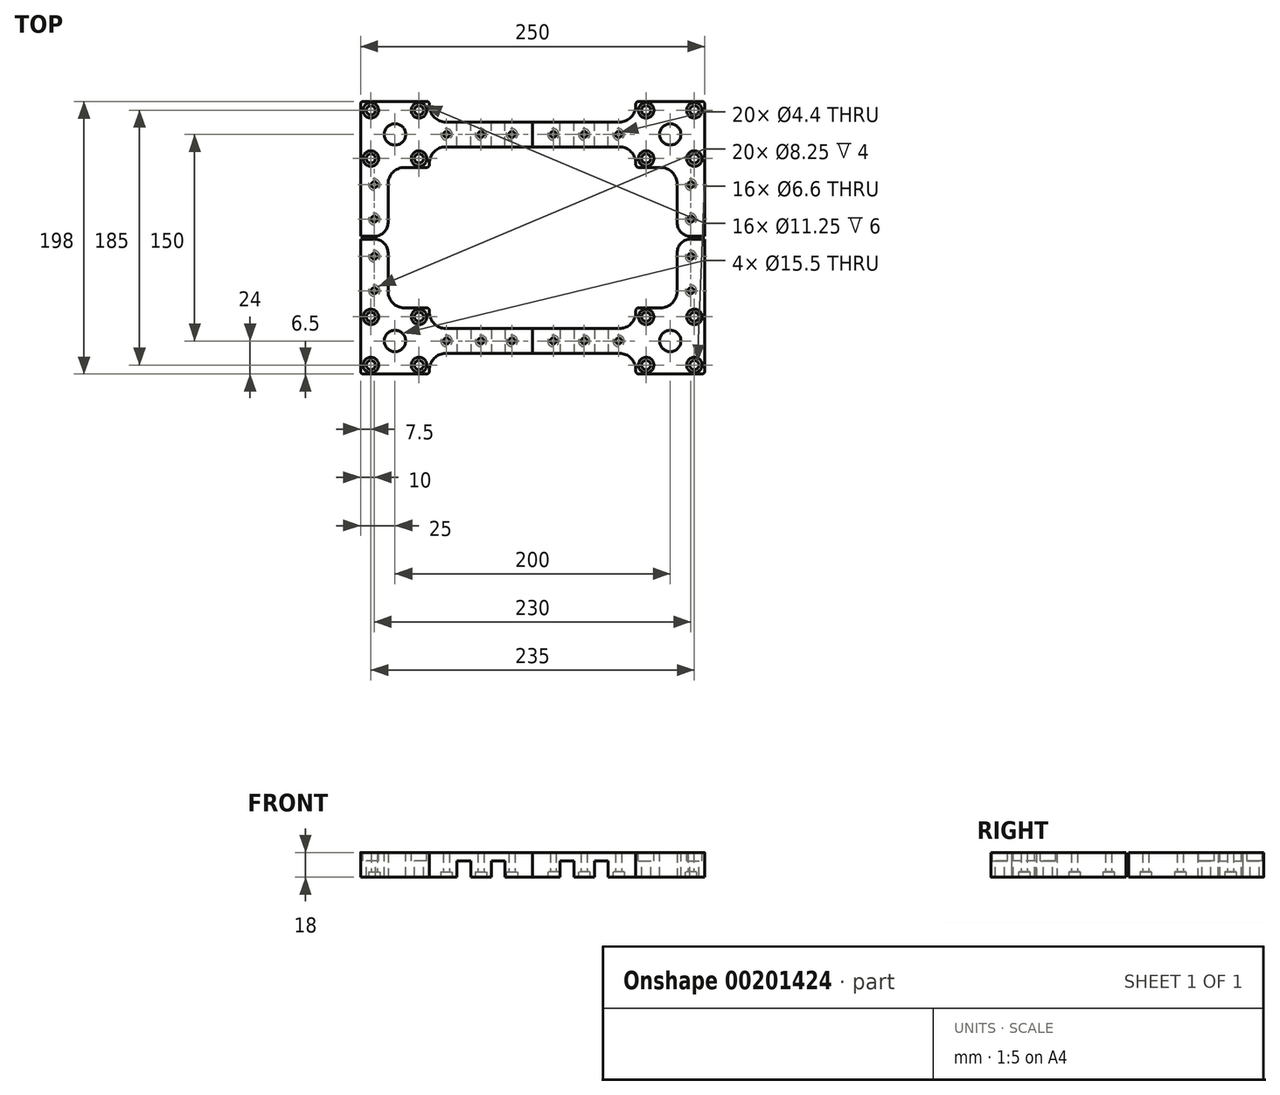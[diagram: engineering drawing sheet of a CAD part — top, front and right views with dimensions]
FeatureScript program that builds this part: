
annotation { "Feature Type Name" : "Feature", "Feature Type Description" : "" }
export const myFeature = defineFeature(function(context is Context, id is Id, definition is map)
    precondition{}
    {
        {
            var Q0;
            Q0=qCreatedBy(makeId("Top.planeOp"),FACE);
            var sketch = newSketch(context, id + "F0", { "sketchPlane" : qUnion([Q0])});
            skLineSegment(sketch, "E0", {"start": v(-125, 0) * mm, "end": v(-125, 24) * mm});
            skLineSegment(sketch, "E1", {"start": v(-105, 24) * mm, "end": v(-75, 24) * mm});
            skLineSegment(sketch, "E2", {"start": v(-75, 24) * mm, "end": v(-75, 9) * mm});
            skLineSegment(sketch, "E3", {"start": v(-75, 9) * mm, "end": v(0, 9) * mm});
            skLineSegment(sketch, "E4", {"start": v(0, 9) * mm, "end": v(0, 0) * mm});
            skLineSegment(sketch, "E5", {"start": v(-125, 24) * mm, "end": v(-125, 74) * mm});
            skLineSegment(sketch, "E6", {"start": v(-105, 74) * mm, "end": v(-125, 74) * mm});
            skLineSegment(sketch, "E7", {"start": v(-105, 74) * mm, "end": v(-105, 24) * mm});
            skLineSegment(sketch, "E8.MirrorCS", {"start": v(-75, -24) * mm, "end": v(-75, -9) * mm});
            skLineSegment(sketch, "E9.MirrorCS", {"start": v(-75, -9) * mm, "end": v(0, -9) * mm});
            skLineSegment(sketch, "E10.MirrorCS", {"start": v(-125, -24) * mm, "end": v(-75, -24) * mm});
            skLineSegment(sketch, "E11.MirrorCS", {"start": v(0, -9) * mm, "end": v(0, 0) * mm});
            skLineSegment(sketch, "E12.MirrorCS", {"start": v(-125, 0) * mm, "end": v(-125, -24) * mm});
            skSolve(sketch);
        }
        {
            var Q0;
            Q0=makeQuery(id+"F0.imprint","IMPRINT",FACE,{"disambiguationData":[TD([[makeQuery(id+"F0.imprint","IMPRINT",EDGE,{"derivedFrom":sQuery(id+"F0.wireOp",EDGE,"E0")}),-1.0]])]});
            extrude(context, id + "F1", {"entities" : qUnion([Q0]), "depth" : 18 * mm});
        }
        {
            var Q0;
            Q0=makeQuery(id+"F1.opExtrude","CAP_FACE",FACE,{"disambiguationData":[OSD([sQuery(id+"F0.wireOp",EDGE,"E0"),sQuery(id+"F0.wireOp",EDGE,"E1"),sQuery(id+"F0.wireOp",EDGE,"E2"),sQuery(id+"F0.wireOp",EDGE,"E3"),sQuery(id+"F0.wireOp",EDGE,"E4"),sQuery(id+"F0.wireOp",EDGE,"E5"),sQuery(id+"F0.wireOp",EDGE,"E6"),sQuery(id+"F0.wireOp",EDGE,"E7"),sQuery(id+"F0.wireOp",EDGE,"E8.MirrorCS"),sQuery(id+"F0.wireOp",EDGE,"E9.MirrorCS"),sQuery(id+"F0.wireOp",EDGE,"E10.MirrorCS"),sQuery(id+"F0.wireOp",EDGE,"E11.MirrorCS"),sQuery(id+"F0.wireOp",EDGE,"E12.MirrorCS")])],"isStart":false});
            var sketch = newSketch(context, id + "F2", { "sketchPlane" : qUnion([Q0])});
            skPoint(sketch, "E13", {"position": v(-117.5, 17.5) * mm});
            skPoint(sketch, "E14", {"position": v(-82.5, 17.5) * mm});
            skPoint(sketch, "E15", {"position": v(-82.5, -17.5) * mm});
            skPoint(sketch, "E16", {"position": v(-117.5, -17.5) * mm});
            skPoint(sketch, "E17", {"position": v(-100, 0) * mm});
            skPoint(sketch, "E18", {"position": v(-15, 0) * mm});
            skPoint(sketch, "E19", {"position": v(-37.5, 0) * mm});
            skPoint(sketch, "E20", {"position": v(-62.5, 0) * mm});
            skPoint(sketch, "E21", {"position": v(-115, 61.5) * mm});
            skPoint(sketch, "E22", {"position": v(-115, 36.5) * mm});
            skSolve(sketch);
        }
        {
            var Q0;
            Q0=sQuery(id+"F2.wireOp",VERTEX,"E13");
            var Q1;
            Q1=sQuery(id+"F2.wireOp",VERTEX,"E14");
            var Q2;
            Q2=sQuery(id+"F2.wireOp",VERTEX,"E15");
            var Q3;
            Q3=sQuery(id+"F2.wireOp",VERTEX,"E16");
            var Q4;
            Q4=makeQuery(id+"F1.opExtrude","SWEPT_BODY",BODY,{"disambiguationData":[OSD([sQuery(id+"F0.wireOp",EDGE,"E0"),sQuery(id+"F0.wireOp",EDGE,"E1"),sQuery(id+"F0.wireOp",EDGE,"E2"),sQuery(id+"F0.wireOp",EDGE,"E3"),sQuery(id+"F0.wireOp",EDGE,"E4"),sQuery(id+"F0.wireOp",EDGE,"E5"),sQuery(id+"F0.wireOp",EDGE,"E6"),sQuery(id+"F0.wireOp",EDGE,"E7"),sQuery(id+"F0.wireOp",EDGE,"E8.MirrorCS"),sQuery(id+"F0.wireOp",EDGE,"E9.MirrorCS"),sQuery(id+"F0.wireOp",EDGE,"E10.MirrorCS"),sQuery(id+"F0.wireOp",EDGE,"E11.MirrorCS"),sQuery(id+"F0.wireOp",EDGE,"E12.MirrorCS")])]});
            hole(context, id + "F3", {"style" : HoleStyle.C_BORE, "endStyle" : HoleEndStyle.THROUGH, "standardTappedOrClearance" : lookupTablePath({ "standard" : "ISO", "fit" : "Normal", "size" : "M6", "type" : "Clearance" }), "standardBlindInLast" : lookupTablePath({ "fit" : "Standard", "standard" : "ISO", "size" : "M6", "type" : "Clearance" }), "holeDiameter" : 6.6 * mm, "cBoreDiameter" : 11.25 * mm, "cBoreDepth" : 6 * mm, "startFromSketch" : true, "locations" : qUnion([Q0, Q1, Q2, Q3]), "scope" : qUnion([Q4]), "isTappedThrough" : true});
        }
        {
            var Q0;
            Q0=makeQuery(id+"F1.opExtrude","CAP_FACE",FACE,{"disambiguationData":[OSD([sQuery(id+"F0.wireOp",EDGE,"E0"),sQuery(id+"F0.wireOp",EDGE,"E1"),sQuery(id+"F0.wireOp",EDGE,"E2"),sQuery(id+"F0.wireOp",EDGE,"E3"),sQuery(id+"F0.wireOp",EDGE,"E4"),sQuery(id+"F0.wireOp",EDGE,"E5"),sQuery(id+"F0.wireOp",EDGE,"E6"),sQuery(id+"F0.wireOp",EDGE,"E7"),sQuery(id+"F0.wireOp",EDGE,"E8.MirrorCS"),sQuery(id+"F0.wireOp",EDGE,"E9.MirrorCS"),sQuery(id+"F0.wireOp",EDGE,"E10.MirrorCS"),sQuery(id+"F0.wireOp",EDGE,"E11.MirrorCS"),sQuery(id+"F0.wireOp",EDGE,"E12.MirrorCS")])],"isStart":true});
            var sketch = newSketch(context, id + "F4", { "sketchPlane" : qUnion([Q0])});
            skPoint(sketch, "E23", {"position": v(-62.5, 0) * mm});
            skPoint(sketch, "E24", {"position": v(-37.5, 0) * mm});
            skPoint(sketch, "E25", {"position": v(-15, 0) * mm});
            skPoint(sketch, "E26", {"position": v(-115, -36.5) * mm});
            skPoint(sketch, "E27", {"position": v(-115, -61.5) * mm});
            skSolve(sketch);
        }
        {
            var Q0;
            Q0=sQuery(id+"F4.wireOp",VERTEX,"E23");
            var Q1;
            Q1=sQuery(id+"F4.wireOp",VERTEX,"E24");
            var Q2;
            Q2=sQuery(id+"F4.wireOp",VERTEX,"E25");
            var Q3;
            Q3=sQuery(id+"F4.wireOp",VERTEX,"E26");
            var Q4;
            Q4=sQuery(id+"F4.wireOp",VERTEX,"E27");
            var Q5;
            Q5=makeQuery(id+"F1.opExtrude","SWEPT_BODY",BODY,{"disambiguationData":[OSD([sQuery(id+"F0.wireOp",EDGE,"E0"),sQuery(id+"F0.wireOp",EDGE,"E1"),sQuery(id+"F0.wireOp",EDGE,"E2"),sQuery(id+"F0.wireOp",EDGE,"E3"),sQuery(id+"F0.wireOp",EDGE,"E4"),sQuery(id+"F0.wireOp",EDGE,"E5"),sQuery(id+"F0.wireOp",EDGE,"E6"),sQuery(id+"F0.wireOp",EDGE,"E7"),sQuery(id+"F0.wireOp",EDGE,"E8.MirrorCS"),sQuery(id+"F0.wireOp",EDGE,"E9.MirrorCS"),sQuery(id+"F0.wireOp",EDGE,"E10.MirrorCS"),sQuery(id+"F0.wireOp",EDGE,"E11.MirrorCS"),sQuery(id+"F0.wireOp",EDGE,"E12.MirrorCS")])]});
            hole(context, id + "F5", {"style" : HoleStyle.C_BORE, "endStyle" : HoleEndStyle.THROUGH, "standardTappedOrClearance" : lookupTablePath({ "standard" : "ISO", "fit" : "Normal", "size" : "M4", "type" : "Clearance" }), "standardBlindInLast" : lookupTablePath({ "fit" : "Standard", "standard" : "ISO", "size" : "M4", "type" : "Clearance" }), "holeDiameter" : 4.4 * mm, "cBoreDiameter" : 8.25 * mm, "cBoreDepth" : 4 * mm, "startFromSketch" : true, "locations" : qUnion([Q0, Q1, Q2, Q3, Q4]), "scope" : qUnion([Q5]), "isTappedThrough" : true});
        }
        {
            var Q0;
            Q0=sQuery(id+"F2.wireOp",VERTEX,"E17");
            var Q1;
            Q1=makeQuery(id+"F1.opExtrude","SWEPT_BODY",BODY,{"disambiguationData":[OSD([sQuery(id+"F0.wireOp",EDGE,"E0"),sQuery(id+"F0.wireOp",EDGE,"E1"),sQuery(id+"F0.wireOp",EDGE,"E2"),sQuery(id+"F0.wireOp",EDGE,"E3"),sQuery(id+"F0.wireOp",EDGE,"E4"),sQuery(id+"F0.wireOp",EDGE,"E5"),sQuery(id+"F0.wireOp",EDGE,"E6"),sQuery(id+"F0.wireOp",EDGE,"E7"),sQuery(id+"F0.wireOp",EDGE,"E8.MirrorCS"),sQuery(id+"F0.wireOp",EDGE,"E9.MirrorCS"),sQuery(id+"F0.wireOp",EDGE,"E10.MirrorCS"),sQuery(id+"F0.wireOp",EDGE,"E11.MirrorCS"),sQuery(id+"F0.wireOp",EDGE,"E12.MirrorCS")])]});
            hole(context, id + "F6", {"style" : HoleStyle.SIMPLE, "endStyle" : HoleEndStyle.THROUGH, "standardTappedOrClearance" : lookupTablePath({ "standard" : "ISO", "fit" : "Normal", "size" : "M14", "type" : "Clearance" }), "standardBlindInLast" : lookupTablePath({ "fit" : "Standard", "standard" : "ISO", "size" : "M14", "type" : "Clearance" }), "holeDiameter" : 15.5 * mm, "startFromSketch" : true, "locations" : qUnion([Q0]), "scope" : qUnion([Q1]), "isTappedThrough" : true});
        }
        {
            var Q0;
            Q0=makeQuery(id+"F1.opExtrude","SWEPT_EDGE",EDGE,{"disambiguationData":[OSD([sQuery(id+"F0.wireOp",EDGE,"E1"),sQuery(id+"F0.wireOp",EDGE,"E7")])]});
            var Q1;
            Q1=makeQuery(id+"F1.opExtrude","SWEPT_EDGE",EDGE,{"disambiguationData":[OSD([sQuery(id+"F0.wireOp",EDGE,"E8.MirrorCS"),sQuery(id+"F0.wireOp",EDGE,"E9.MirrorCS")])]});
            var Q2;
            Q2=makeQuery(id+"F1.opExtrude","SWEPT_EDGE",EDGE,{"disambiguationData":[OSD([sQuery(id+"F0.wireOp",EDGE,"E2"),sQuery(id+"F0.wireOp",EDGE,"E3")])]});
            fillet(context, id + "F7", {"entities" : qUnion([Q0, Q1, Q2]), "radius" : 12 * mm, "tangentPropagation" : true, "allowEdgeOverflow" : false});
        }
        {
            var Q0;
            Q0=makeQuery(id+"F1.opExtrude","SWEPT_EDGE",EDGE,{"disambiguationData":[OSD([sQuery(id+"F0.wireOp",EDGE,"E6"),sQuery(id+"F0.wireOp",EDGE,"E7")])]});
            fillet(context, id + "F8", {"entities" : qUnion([Q0]), "radius" : 10 * mm, "tangentPropagation" : true, "allowEdgeOverflow" : false});
        }
        {
            var Q0;
            Q0=makeQuery(id+"F1.opExtrude","SWEPT_EDGE",EDGE,{"disambiguationData":[OSD([sQuery(id+"F0.wireOp",EDGE,"E1"),sQuery(id+"F0.wireOp",EDGE,"E2")])]});
            fillet(context, id + "F9", {"entities" : qUnion([Q0]), "radius" : 2 * mm, "tangentPropagation" : true, "allowEdgeOverflow" : false});
        }
        {
            var Q0;
            Q0=makeQuery(id+"F1.opExtrude","SWEPT_EDGE",EDGE,{"disambiguationData":[OSD([sQuery(id+"F0.wireOp",EDGE,"E8.MirrorCS"),sQuery(id+"F0.wireOp",EDGE,"E10.MirrorCS")])]});
            var Q1;
            Q1=makeQuery(id+"F1.opExtrude","SWEPT_EDGE",EDGE,{"disambiguationData":[OSD([sQuery(id+"F0.wireOp",EDGE,"E10.MirrorCS"),sQuery(id+"F0.wireOp",EDGE,"E12.MirrorCS")])]});
            fillet(context, id + "F10", {"entities" : qUnion([Q0, Q1]), "radius" : 2 * mm, "tangentPropagation" : true, "allowEdgeOverflow" : false});
        }
        {
            var Q0;
            Q0=makeQuery(id+"F1.opExtrude","SWEPT_FACE",FACE,{"disambiguationData":[OSD([sQuery(id+"F0.wireOp",EDGE,"E9.MirrorCS")])]});
            var sketch = newSketch(context, id + "F11", { "sketchPlane" : qUnion([Q0])});
            skLineSegment(sketch, "E28.bottom", {"start": v(-55, 12) * mm, "end": v(-45, 12) * mm});
            skLineSegment(sketch, "E28.top", {"start": v(-55, 0) * mm, "end": v(-45, 0) * mm});
            skLineSegment(sketch, "E28.left", {"start": v(-55, 12) * mm, "end": v(-55, 0) * mm});
            skLineSegment(sketch, "E28.right", {"start": v(-45, 12) * mm, "end": v(-45, 0) * mm});
            skLineSegment(sketch, "E29.1.0.0", {"start": v(-20, 12) * mm, "end": v(-20, 0) * mm});
            skLineSegment(sketch, "E29.1.0.1", {"start": v(-30, 0) * mm, "end": v(-20, 0) * mm});
            skLineSegment(sketch, "E29.1.0.2", {"start": v(-30, 12) * mm, "end": v(-30, 0) * mm});
            skLineSegment(sketch, "E29.1.0.3", {"start": v(-30, 12) * mm, "end": v(-20, 12) * mm});
            skLineSegment(sketch, "E29.direction1", {"start": v(-55, 0) * mm, "end": v(-30, 0) * mm, "construction": true});
            skSolve(sketch);
        }
        {
            var Q0;
            Q0=makeQuery(id+"F11.imprint","IMPRINT",FACE,{"disambiguationData":[TD([[makeQuery(id+"F11.imprint","IMPRINT",EDGE,{"derivedFrom":sQuery(id+"F11.wireOp",EDGE,"E28.bottom")}),-1.0]])]});
            var Q1;
            Q1=makeQuery(id+"F11.imprint","IMPRINT",FACE,{"disambiguationData":[TD([[makeQuery(id+"F11.imprint","IMPRINT",EDGE,{"derivedFrom":sQuery(id+"F11.wireOp",EDGE,"E29.1.0.0")}),-1.0]])]});
            extrude(context, id + "F12", {"entities" : qUnion([Q0, Q1]), "operationType" : NewBodyOperationType.REMOVE, "endBound" : BoundingType.THROUGH_ALL, "oppositeDirection" : true, "depth" : 25 * mm});
        }
        {
            var Q0;
            Q0=makeQuery(id+"F1.opExtrude","SWEPT_BODY",BODY,{"disambiguationData":[OSD([sQuery(id+"F0.wireOp",EDGE,"E0"),sQuery(id+"F0.wireOp",EDGE,"E1"),sQuery(id+"F0.wireOp",EDGE,"E2"),sQuery(id+"F0.wireOp",EDGE,"E3"),sQuery(id+"F0.wireOp",EDGE,"E4"),sQuery(id+"F0.wireOp",EDGE,"E5"),sQuery(id+"F0.wireOp",EDGE,"E6"),sQuery(id+"F0.wireOp",EDGE,"E7"),sQuery(id+"F0.wireOp",EDGE,"E8.MirrorCS"),sQuery(id+"F0.wireOp",EDGE,"E9.MirrorCS"),sQuery(id+"F0.wireOp",EDGE,"E10.MirrorCS"),sQuery(id+"F0.wireOp",EDGE,"E11.MirrorCS"),sQuery(id+"F0.wireOp",EDGE,"E12.MirrorCS")])]});
            var Q1;
            Q1=qCreatedBy(makeId("Right.planeOp"),FACE);
            mirror(context, id + "F13", {"entities" : qUnion([Q0]), "mirrorPlane" : qUnion([Q1])});
        }
        {
            var Q0;
            Q0=makeQuery(id+"F1.opExtrude","SWEPT_BODY",BODY,{"disambiguationData":[OSD([sQuery(id+"F0.wireOp",EDGE,"E0"),sQuery(id+"F0.wireOp",EDGE,"E1"),sQuery(id+"F0.wireOp",EDGE,"E2"),sQuery(id+"F0.wireOp",EDGE,"E3"),sQuery(id+"F0.wireOp",EDGE,"E4"),sQuery(id+"F0.wireOp",EDGE,"E5"),sQuery(id+"F0.wireOp",EDGE,"E6"),sQuery(id+"F0.wireOp",EDGE,"E7"),sQuery(id+"F0.wireOp",EDGE,"E8.MirrorCS"),sQuery(id+"F0.wireOp",EDGE,"E9.MirrorCS"),sQuery(id+"F0.wireOp",EDGE,"E10.MirrorCS"),sQuery(id+"F0.wireOp",EDGE,"E11.MirrorCS"),sQuery(id+"F0.wireOp",EDGE,"E12.MirrorCS")])]});
            var Q1;
            Q1=qCreatedBy(makeId("Front.planeOp"),FACE);
            mirror(context, id + "F14", {"entities" : qUnion([Q0]), "mirrorPlane" : qUnion([Q1])});
        }
        {
            var Q0;
            Q0=makeQuery(id+"F13.opPattern","COPY",BODY,{"derivedFrom":makeQuery(id+"F1.opExtrude","SWEPT_BODY",BODY,{"disambiguationData":[OSD([sQuery(id+"F0.wireOp",EDGE,"E0"),sQuery(id+"F0.wireOp",EDGE,"E1"),sQuery(id+"F0.wireOp",EDGE,"E2"),sQuery(id+"F0.wireOp",EDGE,"E3"),sQuery(id+"F0.wireOp",EDGE,"E4"),sQuery(id+"F0.wireOp",EDGE,"E5"),sQuery(id+"F0.wireOp",EDGE,"E6"),sQuery(id+"F0.wireOp",EDGE,"E7"),sQuery(id+"F0.wireOp",EDGE,"E8.MirrorCS"),sQuery(id+"F0.wireOp",EDGE,"E9.MirrorCS"),sQuery(id+"F0.wireOp",EDGE,"E10.MirrorCS"),sQuery(id+"F0.wireOp",EDGE,"E11.MirrorCS"),sQuery(id+"F0.wireOp",EDGE,"E12.MirrorCS")])]}),"instanceName":"1"});
            var Q1;
            Q1=qCreatedBy(makeId("Front.planeOp"),FACE);
            mirror(context, id + "F15", {"entities" : qUnion([Q0]), "mirrorPlane" : qUnion([Q1])});
        }
        {
            var Q0;
            Q0=makeQuery(id+"F13.opPattern","COPY",BODY,{"derivedFrom":makeQuery(id+"F1.opExtrude","SWEPT_BODY",BODY,{"disambiguationData":[OSD([sQuery(id+"F0.wireOp",EDGE,"E0"),sQuery(id+"F0.wireOp",EDGE,"E1"),sQuery(id+"F0.wireOp",EDGE,"E2"),sQuery(id+"F0.wireOp",EDGE,"E3"),sQuery(id+"F0.wireOp",EDGE,"E4"),sQuery(id+"F0.wireOp",EDGE,"E5"),sQuery(id+"F0.wireOp",EDGE,"E6"),sQuery(id+"F0.wireOp",EDGE,"E7"),sQuery(id+"F0.wireOp",EDGE,"E8.MirrorCS"),sQuery(id+"F0.wireOp",EDGE,"E9.MirrorCS"),sQuery(id+"F0.wireOp",EDGE,"E10.MirrorCS"),sQuery(id+"F0.wireOp",EDGE,"E11.MirrorCS"),sQuery(id+"F0.wireOp",EDGE,"E12.MirrorCS")])]}),"instanceName":"1"});
            transform(context, id + "F16", {"entities" : qUnion([Q0]), "transformType" : TransformType.TRANSLATION_3D, "dx" : 0 * mm, "dy" : -150 * mm, "dz" : 0 * mm, "makeCopy" : false});
        }
        {
            var Q0;
            Q0=makeQuery(id+"F1.opExtrude","SWEPT_BODY",BODY,{"disambiguationData":[OSD([sQuery(id+"F0.wireOp",EDGE,"E0"),sQuery(id+"F0.wireOp",EDGE,"E1"),sQuery(id+"F0.wireOp",EDGE,"E2"),sQuery(id+"F0.wireOp",EDGE,"E3"),sQuery(id+"F0.wireOp",EDGE,"E4"),sQuery(id+"F0.wireOp",EDGE,"E5"),sQuery(id+"F0.wireOp",EDGE,"E6"),sQuery(id+"F0.wireOp",EDGE,"E7"),sQuery(id+"F0.wireOp",EDGE,"E8.MirrorCS"),sQuery(id+"F0.wireOp",EDGE,"E9.MirrorCS"),sQuery(id+"F0.wireOp",EDGE,"E10.MirrorCS"),sQuery(id+"F0.wireOp",EDGE,"E11.MirrorCS"),sQuery(id+"F0.wireOp",EDGE,"E12.MirrorCS")])]});
            transform(context, id + "F17", {"entities" : qUnion([Q0]), "transformType" : TransformType.TRANSLATION_3D, "dx" : 0 * mm, "dy" : -150 * mm, "dz" : 0 * mm, "makeCopy" : false});
        }
    });
